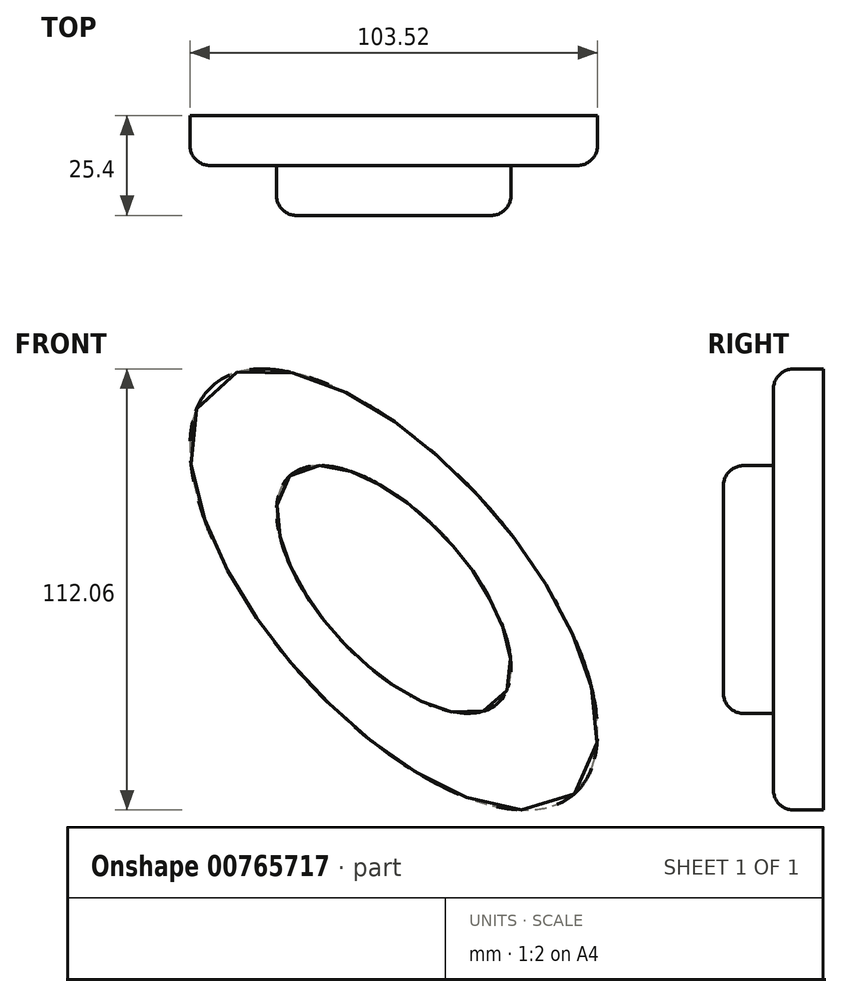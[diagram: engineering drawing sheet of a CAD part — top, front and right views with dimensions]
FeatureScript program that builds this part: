
annotation { "Feature Type Name" : "Feature", "Feature Type Description" : "" }
export const myFeature = defineFeature(function(context is Context, id is Id, definition is map)
    precondition{}
    {
        {
            var Q0;
            Q0=qCreatedBy(makeId("Front.planeOp"),FACE);
            var sketch = newSketch(context, id + "F0", { "sketchPlane" : qUnion([Q0])});
            skEllipse(sketch, "E0", {"center": v(0, 0) * mm, "majorRadius": 69.29 * mm, "minorRadius": 31.91 * mm, "majorAxis": v(0.66, -0.75)});
            skSolve(sketch);
        }
        {
            var Q0;
            Q0 = qSketchRegion(id + "F0", true);
            extrude(context, id + "F1", {"entities" : qUnion([Q0]), "oppositeDirection" : true, "depth" : 12.7 * mm, "offsetDistance" : 25.4 * mm});
        }
        {
            var Q0;
            Q0=makeQuery(id+"F0.imprint","IMPRINT",FACE,{"disambiguationData":[TD([[makeQuery(id+"F0.imprint","IMPRINT",EDGE,{"derivedFrom":sQuery(id+"F0.wireOp",EDGE,"E0")}),1.0]])]});
            var sketch = newSketch(context, id + "F2", { "sketchPlane" : qUnion([Q0])});
            skEllipse(sketch, "E1", {"center": v(0, 0) * mm, "majorRadius": 39.13 * mm, "minorRadius": 18.6 * mm, "majorAxis": v(-0.68, 0.74)});
            skSolve(sketch);
        }
        {
            var Q0;
            Q0 = qSketchRegion(id + "F2", true);
            extrude(context, id + "F3", {"entities" : qUnion([Q0]), "operationType" : NewBodyOperationType.ADD, "depth" : 12.7 * mm, "offsetDistance" : 25.4 * mm});
        }
        {
            var Q0;
            Q0=makeQuery(id+"F1.opExtrude","CAP_EDGE",EDGE,{"disambiguationData":[OSD([sQuery(id+"F0.wireOp",EDGE,"E0")])],"isStart":true});
            var Q1;
            Q1=makeQuery(id+"F3.opExtrude","CAP_FACE",FACE,{"disambiguationData":[OSD([sQuery(id+"F2.wireOp",EDGE,"E1")])],"isStart":false});
            fillet(context, id + "F4", {"entities" : qUnion([Q0, Q1]), "radius" : 5.08 * mm, "tangentPropagation" : true, "allowEdgeOverflow" : false});
        }
    });
